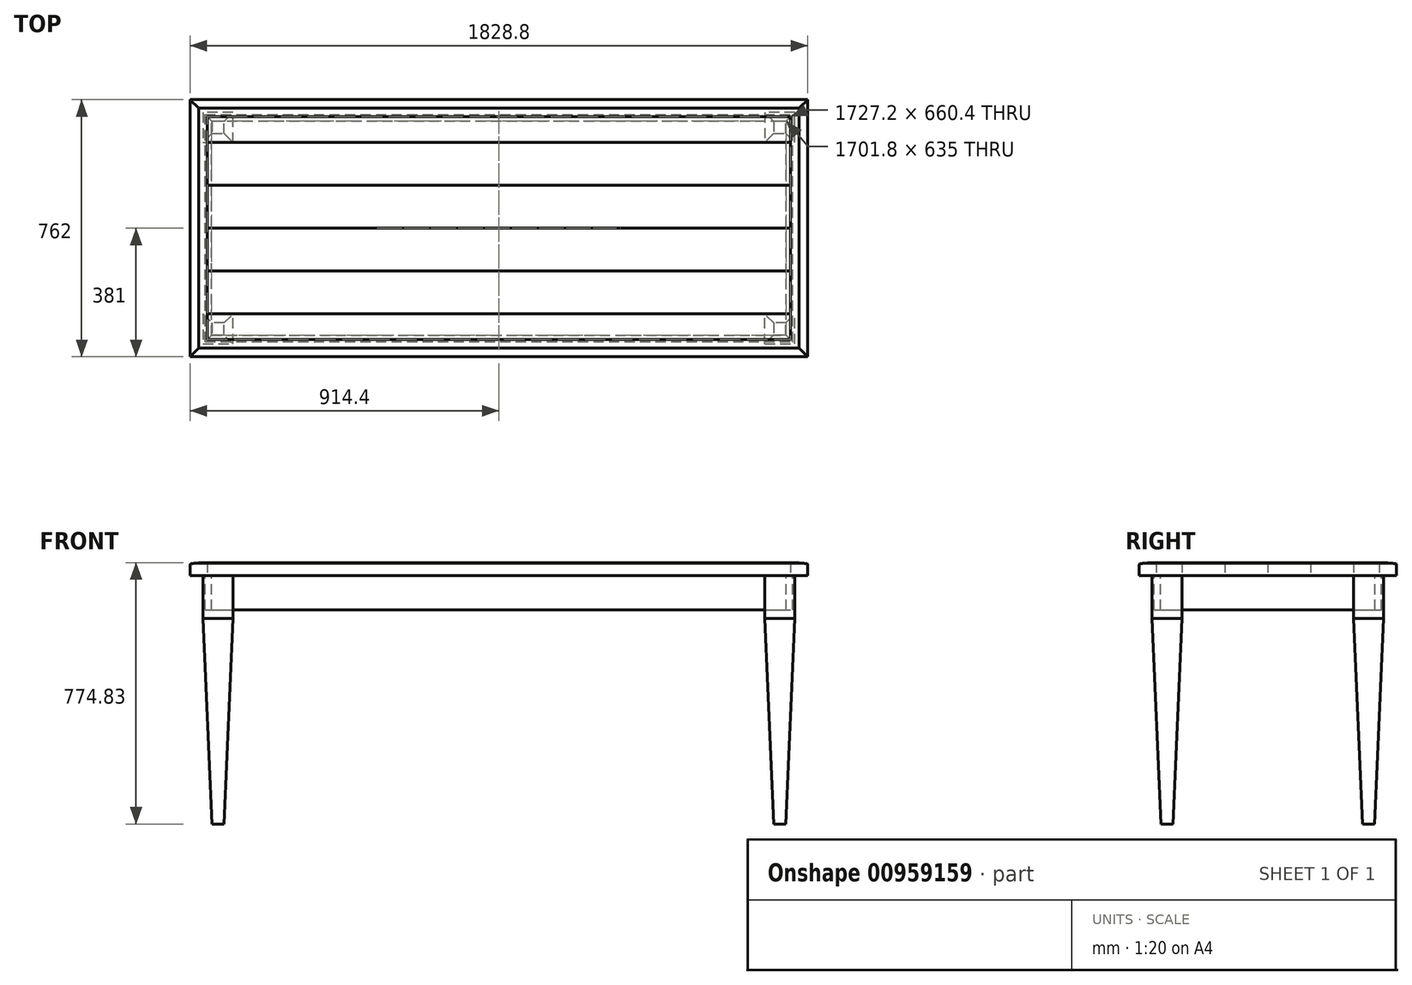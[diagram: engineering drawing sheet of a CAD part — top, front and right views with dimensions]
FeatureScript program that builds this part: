
annotation { "Feature Type Name" : "Feature", "Feature Type Description" : "" }
export const myFeature = defineFeature(function(context is Context, id is Id, definition is map)
    precondition{}
    {
        {
            var Q0;
            Q0=qCreatedBy(makeId("Top.planeOp"),FACE);
            var sketch = newSketch(context, id + "F0", { "sketchPlane" : qUnion([Q0])});
            skLineSegment(sketch, "E0.bottom", {"start": v(-863.6, 330.2) * mm, "end": v(863.6, 330.2) * mm});
            skLineSegment(sketch, "E0.top", {"start": v(-863.6, -330.2) * mm, "end": v(863.6, -330.2) * mm});
            skLineSegment(sketch, "E0.left", {"start": v(-863.6, 330.2) * mm, "end": v(-863.6, -330.2) * mm});
            skLineSegment(sketch, "E0.right", {"start": v(863.6, 330.2) * mm, "end": v(863.6, -330.2) * mm});
            skPoint(sketch, "E0.middle", {"position": v(0, 0) * mm});
            skLineSegment(sketch, "E1", {"start": v(-863.6, 254) * mm, "end": v(863.6, 254) * mm});
            skLineSegment(sketch, "E2.0.1.0", {"start": v(-863.6, 127) * mm, "end": v(863.6, 127) * mm});
            skLineSegment(sketch, "E2.0.2.0", {"start": v(-863.6, 0) * mm, "end": v(863.6, 0) * mm});
            skLineSegment(sketch, "E2.0.3.0", {"start": v(-863.6, -127) * mm, "end": v(863.6, -127) * mm});
            skLineSegment(sketch, "E2.0.4.0", {"start": v(-863.6, -254) * mm, "end": v(863.6, -254) * mm});
            skLineSegment(sketch, "E2.direction1", {"start": v(-863.6, 254) * mm, "end": v(-863.6, 254) * mm});
            skLineSegment(sketch, "E2.direction2", {"start": v(-863.6, 254) * mm, "end": v(-863.6, 127) * mm, "construction": true});
            skSolve(sketch);
        }
        {
            var Q0;
            {var subQ0=sQuery(id+"F0.wireOp",EDGE,"E0.bottom");Q0=makeQuery(id+"F0.imprint","IMPRINT",FACE,{"disambiguationData":[TD([[makeQuery(id+"F0.imprint","IMPRINT",EDGE,{"derivedFrom":subQ0}),-1.0]])]});}
            var Q1;
            {var subQ0=sQuery(id+"F0.wireOp",EDGE,"E2.0.1.0");Q1=makeQuery(id+"F0.imprint","IMPRINT",FACE,{"disambiguationData":[TD([[makeQuery(id+"F0.imprint","IMPRINT",EDGE,{"derivedFrom":subQ0}),-1.0]])]});}
            var Q2;
            {var subQ0=sQuery(id+"F0.wireOp",EDGE,"E2.0.3.0");Q2=makeQuery(id+"F0.imprint","IMPRINT",FACE,{"disambiguationData":[TD([[makeQuery(id+"F0.imprint","IMPRINT",EDGE,{"derivedFrom":subQ0}),-1.0]])]});}
            extrude(context, id + "F1", {"entities" : qUnion([Q0, Q1, Q2]), "depth" : 38.1 * mm, "offsetDistance" : 25.4 * mm});
        }
        {
            var Q0;
            {var subQ0=sQuery(id+"F0.wireOp",EDGE,"E1");Q0=makeQuery(id+"F0.imprint","IMPRINT",FACE,{"disambiguationData":[TD([[makeQuery(id+"F0.imprint","IMPRINT",EDGE,{"derivedFrom":subQ0}),-1.0]])]});}
            var Q1;
            {var subQ0=sQuery(id+"F0.wireOp",EDGE,"E2.0.2.0");Q1=makeQuery(id+"F0.imprint","IMPRINT",FACE,{"disambiguationData":[TD([[makeQuery(id+"F0.imprint","IMPRINT",EDGE,{"derivedFrom":subQ0}),-1.0]])]});}
            var Q2;
            {var subQ0=sQuery(id+"F0.wireOp",EDGE,"E0.top");Q2=makeQuery(id+"F0.imprint","IMPRINT",FACE,{"disambiguationData":[TD([[makeQuery(id+"F0.imprint","IMPRINT",EDGE,{"derivedFrom":subQ0}),1.0]])]});}
            extrude(context, id + "F2", {"entities" : qUnion([Q0, Q1, Q2]), "depth" : 38.23 * mm, "offsetDistance" : 25.4 * mm});
        }
        {
            var Q0;
            Q0=qCreatedBy(makeId("Right.planeOp"),FACE);
            var sketch = newSketch(context, id + "F3", { "sketchPlane" : qUnion([Q0])});
            skLineSegment(sketch, "E3", {"start": v(-329.63, 0) * mm, "end": v(-381, 0) * mm});
            skLineSegment(sketch, "E4", {"start": v(-147, 139.44) * mm, "end": v(-147, 139.44) * mm});
            skLineSegment(sketch, "E5", {"start": v(-140.65, 145.8) * mm, "end": v(-140.65, 145.8) * mm});
            skLineSegment(sketch, "E6", {"start": v(-355.6, 38.1) * mm, "end": v(-330.2, 38.1) * mm});
            skPoint(sketch, "E7.visualSharp", {"position": v(-396.17, 38.1) * mm});
            skPoint(sketch, "E8.visualSharp", {"position": v(-396.17, 6.35) * mm});
            skLineSegment(sketch, "E9", {"start": v(-330.2, 38.1) * mm, "end": v(-330.2, 0) * mm});
            skLineSegment(sketch, "E10", {"start": v(-355.6, 38.1) * mm, "end": v(-355.6, 36.51) * mm});
            skLineSegment(sketch, "E11", {"start": v(-381, 0) * mm, "end": v(-381, 28.58) * mm});
            skFitSpline(sketch, "E12", {"points": [v(-355.6, 36.51) * mm, v(-377.44, 35.2) * mm, v(-381, 28.58) * mm], "startDerivative": vector(-24.67, 0) * mm, "endDerivative": vector(0, -43.23) * mm});
            skLineSegment(sketch, "E13", {"start": v(-358.08, 36.51) * mm, "end": v(-355.6, 36.51) * mm, "construction": true});
            skSolve(sketch);
        }
        {
            var Q0;
            Q0=makeQuery(id+"F3.imprint","IMPRINT",FACE,{"disambiguationData":[TD([[makeQuery(id+"F3.imprint","IMPRINT",EDGE,{"derivedFrom":sQuery(id+"F3.wireOp",EDGE,"E6")}),-1.0]])]});
            var Q1;
            Q1=sQuery(id+"F0.wireOp",EDGE,"E0.top");
            var Q2;
            Q2=sQuery(id+"F0.wireOp",EDGE,"E0.right");
            var Q3;
            Q3=sQuery(id+"F0.wireOp",EDGE,"E0.bottom");
            var Q4;
            Q4=sQuery(id+"F0.wireOp",EDGE,"E0.left");
            sweep(context, id + "F4", {"profiles" : qUnion([Q0]), "path" : qUnion([Q1, Q2, Q3, Q4])});
        }
        {
            var Q0;
            Q0=qCreatedBy(makeId("Top.planeOp"),FACE);
            var sketch = newSketch(context, id + "F5", { "sketchPlane" : qUnion([Q0])});
            skLineSegment(sketch, "E14.bottom", {"start": v(-787.4, -342.9) * mm, "end": v(-876.3, -342.9) * mm});
            skLineSegment(sketch, "E14.top", {"start": v(-787.4, -254) * mm, "end": v(-876.3, -254) * mm});
            skLineSegment(sketch, "E14.left", {"start": v(-787.4, -342.9) * mm, "end": v(-787.4, -254) * mm});
            skLineSegment(sketch, "E14.right", {"start": v(-876.3, -342.9) * mm, "end": v(-876.3, -254) * mm});
            skPoint(sketch, "E14.middle", {"position": v(-831.85, -298.45) * mm});
            skLineSegment(sketch, "E15.MirrorCS", {"start": v(787.4, -342.9) * mm, "end": v(787.4, -254) * mm});
            skLineSegment(sketch, "E16.MirrorCS", {"start": v(787.4, -342.9) * mm, "end": v(876.3, -342.9) * mm});
            skLineSegment(sketch, "E17.MirrorCS", {"start": v(876.3, -342.9) * mm, "end": v(876.3, -254) * mm});
            skLineSegment(sketch, "E18.MirrorCS", {"start": v(787.4, -254) * mm, "end": v(876.3, -254) * mm});
            skLineSegment(sketch, "E19.MirrorCS", {"start": v(787.4, 342.9) * mm, "end": v(876.3, 342.9) * mm});
            skLineSegment(sketch, "E20.MirrorCS", {"start": v(-787.4, 342.9) * mm, "end": v(-787.4, 254) * mm});
            skLineSegment(sketch, "E21.MirrorCS", {"start": v(787.4, 254) * mm, "end": v(876.3, 254) * mm});
            skLineSegment(sketch, "E22.MirrorCS", {"start": v(-876.3, 342.9) * mm, "end": v(-876.3, 254) * mm});
            skPoint(sketch, "E23.MirrorP", {"position": v(-831.85, 298.45) * mm});
            skLineSegment(sketch, "E24.MirrorCS", {"start": v(-787.4, 342.9) * mm, "end": v(-876.3, 342.9) * mm});
            skLineSegment(sketch, "E25.MirrorCS", {"start": v(-787.4, 254) * mm, "end": v(-876.3, 254) * mm});
            skLineSegment(sketch, "E26.MirrorCS", {"start": v(876.3, 342.9) * mm, "end": v(876.3, 254) * mm});
            skLineSegment(sketch, "E27.MirrorCS", {"start": v(787.4, 342.9) * mm, "end": v(787.4, 254) * mm});
            skSolve(sketch);
        }
        {
            var Q0;
            Q0 = qSketchRegion(id + "F5", true);
            extrude(context, id + "F6", {"entities" : qUnion([Q0]), "oppositeDirection" : true, "depth" : 127 * mm, "offsetDistance" : 25.4 * mm});
        }
        {
            var Q0;
            Q0=qCreatedBy(makeId("Top.planeOp"),FACE);
            var sketch = newSketch(context, id + "F7", { "sketchPlane" : qUnion([Q0])});
            skLineSegment(sketch, "E28.bottom", {"start": v(-869.95, -336.55) * mm, "end": v(869.95, -336.55) * mm});
            skLineSegment(sketch, "E28.top", {"start": v(-869.95, 336.55) * mm, "end": v(869.95, 336.55) * mm});
            skLineSegment(sketch, "E28.left", {"start": v(-869.95, -336.55) * mm, "end": v(-869.95, 336.55) * mm});
            skLineSegment(sketch, "E28.right", {"start": v(869.95, -336.55) * mm, "end": v(869.95, 336.55) * mm});
            skPoint(sketch, "E28.middle", {"position": v(0, 0) * mm});
            skLineSegment(sketch, "E29.0", {"start": v(-850.9, -317.5) * mm, "end": v(850.9, -317.5) * mm});
            skLineSegment(sketch, "E29.1", {"start": v(-850.9, -317.5) * mm, "end": v(-850.9, 317.5) * mm});
            skLineSegment(sketch, "E29.2", {"start": v(-850.9, 317.5) * mm, "end": v(850.9, 317.5) * mm});
            skLineSegment(sketch, "E29.3", {"start": v(850.9, -317.5) * mm, "end": v(850.9, 317.5) * mm});
            skSolve(sketch);
        }
        {
            var Q0;
            Q0 = qSketchRegion(id + "F7", true);
            extrude(context, id + "F8", {"entities" : qUnion([Q0]), "oppositeDirection" : true, "depth" : 101.6 * mm, "offsetDistance" : 25.4 * mm});
        }
        {
            var Q0;
            Q0=makeQuery(id+"F6.opExtrude","CAP_FACE",FACE,{"disambiguationData":[OSD([sQuery(id+"F5.wireOp",EDGE,"E14.bottom"),sQuery(id+"F5.wireOp",EDGE,"E14.top"),sQuery(id+"F5.wireOp",EDGE,"E14.left"),sQuery(id+"F5.wireOp",EDGE,"E14.right")])],"isStart":false});
            var sketch = newSketch(context, id + "F9", { "sketchPlane" : qUnion([Q0])});
            skLineSegment(sketch, "E30.0.0", {"start": v(-787.4, 254) * mm, "end": v(-787.4, 342.9) * mm});
            skLineSegment(sketch, "E30.0.1", {"start": v(-787.4, 342.9) * mm, "end": v(-876.3, 342.9) * mm});
            skLineSegment(sketch, "E30.0.2", {"start": v(-876.3, 342.9) * mm, "end": v(-876.3, 254) * mm});
            skLineSegment(sketch, "E30.0.3", {"start": v(-876.3, 254) * mm, "end": v(-787.4, 254) * mm});
            skLineSegment(sketch, "E31.0.0", {"start": v(787.4, 254) * mm, "end": v(876.3, 254) * mm});
            skLineSegment(sketch, "E31.0.1", {"start": v(876.3, 254) * mm, "end": v(876.3, 342.9) * mm});
            skLineSegment(sketch, "E31.0.2", {"start": v(876.3, 342.9) * mm, "end": v(787.4, 342.9) * mm});
            skLineSegment(sketch, "E31.0.3", {"start": v(787.4, 342.9) * mm, "end": v(787.4, 254) * mm});
            skLineSegment(sketch, "E32.0.0", {"start": v(787.4, -254) * mm, "end": v(787.4, -342.9) * mm});
            skLineSegment(sketch, "E32.0.1", {"start": v(787.4, -342.9) * mm, "end": v(876.3, -342.9) * mm});
            skLineSegment(sketch, "E32.0.2", {"start": v(876.3, -342.9) * mm, "end": v(876.3, -254) * mm});
            skLineSegment(sketch, "E32.0.3", {"start": v(876.3, -254) * mm, "end": v(787.4, -254) * mm});
            skLineSegment(sketch, "E33.0.0", {"start": v(-876.3, -342.9) * mm, "end": v(-787.4, -342.9) * mm});
            skLineSegment(sketch, "E33.0.1", {"start": v(-787.4, -342.9) * mm, "end": v(-787.4, -254) * mm});
            skLineSegment(sketch, "E33.0.2", {"start": v(-787.4, -254) * mm, "end": v(-876.3, -254) * mm});
            skLineSegment(sketch, "E33.0.3", {"start": v(-876.3, -254) * mm, "end": v(-876.3, -342.9) * mm});
            skSolve(sketch);
        }
        {
            var Q0;
            Q0 = qSketchRegion(id + "F9", true);
            extrude(context, id + "F10", {"entities" : qUnion([Q0]), "depth" : 609.6 * mm, "offsetDistance" : 25.4 * mm, "hasDraft" : true, "draftAngle" : 2.5 * degree, "draftPullDirection" : true});
        }
    });
